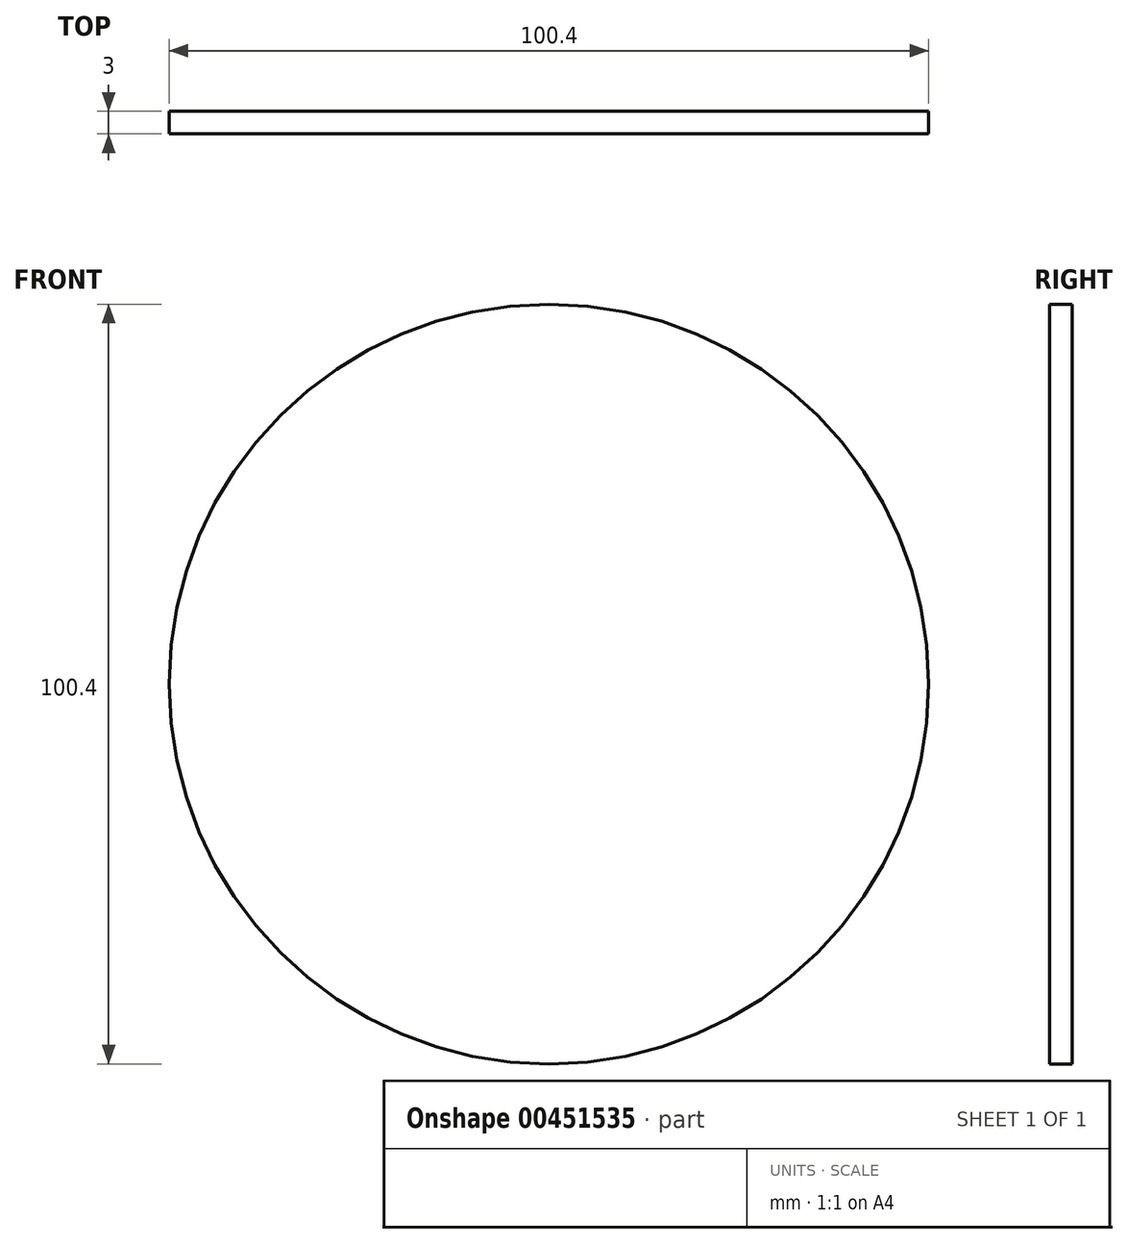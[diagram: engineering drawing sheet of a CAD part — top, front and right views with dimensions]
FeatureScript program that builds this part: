
annotation { "Feature Type Name" : "Feature", "Feature Type Description" : "" }
export const myFeature = defineFeature(function(context is Context, id is Id, definition is map)
    precondition{}
    {
        {
            var Q0;
            Q0=qCreatedBy(makeId("Front.planeOp"),FACE);
            var sketch = newSketch(context, id + "F0", { "sketchPlane" : qUnion([Q0])});
            skCircle(sketch, "E0", {"center": v(0, 0) * mm, "radius": 50.2 * mm});
            skSolve(sketch);
        }
        {
            var Q0;
            Q0=makeQuery(id+"F0.imprint","IMPRINT",FACE,{"disambiguationData":[TD([[makeQuery(id+"F0.imprint","IMPRINT",EDGE,{"derivedFrom":sQuery(id+"F0.wireOp",EDGE,"E0")}),1.0]])]});
            extrude(context, id + "F1", {"entities" : qUnion([Q0]), "depth" : 3 * mm});
        }
    });
